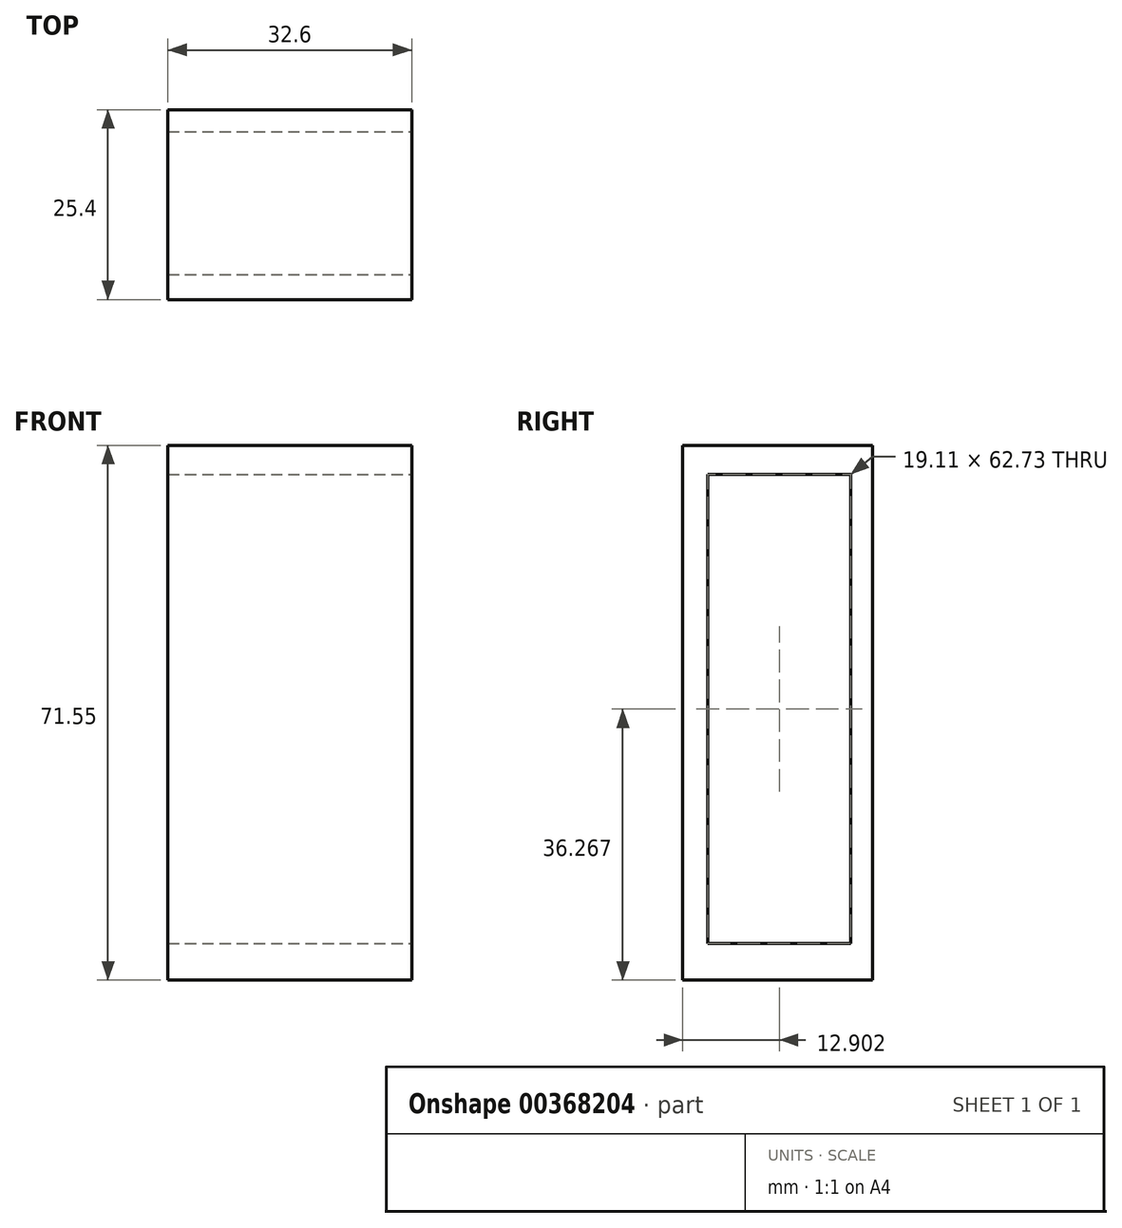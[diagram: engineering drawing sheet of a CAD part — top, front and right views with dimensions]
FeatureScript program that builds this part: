
annotation { "Feature Type Name" : "Feature", "Feature Type Description" : "" }
export const myFeature = defineFeature(function(context is Context, id is Id, definition is map)
    precondition{}
    {
        {
            var Q0;
            Q0=qCreatedBy(makeId("Front.planeOp"),FACE);
            var sketch = newSketch(context, id + "F0", { "sketchPlane" : qUnion([Q0])});
            skLineSegment(sketch, "E0.bottom", {"start": v(-51.95, -15.56) * mm, "end": v(56.85, -15.56) * mm});
            skLineSegment(sketch, "E0.top", {"start": v(-51.95, 56) * mm, "end": v(56.85, 56) * mm});
            skLineSegment(sketch, "E0.left", {"start": v(-51.95, -15.56) * mm, "end": v(-51.95, 56) * mm});
            skLineSegment(sketch, "E0.right", {"start": v(56.85, -15.56) * mm, "end": v(56.85, 56) * mm});
            skSolve(sketch);
        }
        {
            var Q0;
            Q0 = qSketchRegion(id + "F0", true);
            extrude(context, id + "F1", {"entities" : qUnion([Q0]), "depth" : 25.4 * mm});
        }
        {
            var Q0;
            Q0=qCreatedBy(makeId("Right.planeOp"),FACE);
            var sketch = newSketch(context, id + "F2", { "sketchPlane" : qUnion([Q0])});
            skLineSegment(sketch, "E1.bottom", {"start": v(-22.05, 52.07) * mm, "end": v(-2.94, 52.07) * mm});
            skLineSegment(sketch, "E1.top", {"start": v(-22.05, -10.66) * mm, "end": v(-2.94, -10.66) * mm});
            skLineSegment(sketch, "E1.left", {"start": v(-22.05, 52.07) * mm, "end": v(-22.05, -10.66) * mm});
            skLineSegment(sketch, "E1.right", {"start": v(-2.94, 52.07) * mm, "end": v(-2.94, -10.66) * mm});
            skSolve(sketch);
        }
        {
            var Q0;
            Q0=makeQuery(id+"F1.opExtrude","SWEPT_FACE",FACE,{"disambiguationData":[OSD([sQuery(id+"F0.wireOp",EDGE,"E0.right")])]});
            var Q1;
            Q1 = qSketchRegion(id + "F2", true);
            extrude(context, id + "F3", {"entities" : qUnion([Q0, Q1]), "operationType" : NewBodyOperationType.REMOVE, "oppositeDirection" : true, "depth" : 76.2 * mm});
        }
    });
